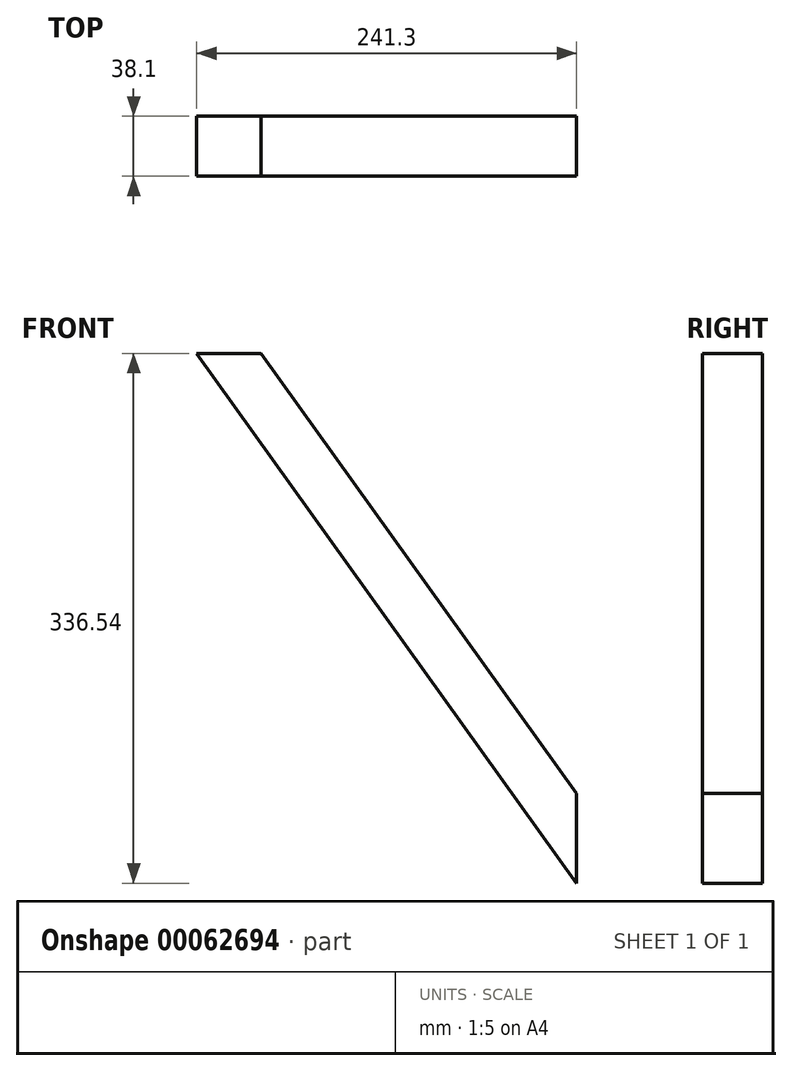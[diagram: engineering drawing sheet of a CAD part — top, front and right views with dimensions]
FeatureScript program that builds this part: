
annotation { "Feature Type Name" : "Feature", "Feature Type Description" : "" }
export const myFeature = defineFeature(function(context is Context, id is Id, definition is map)
    precondition{}
    {
        {
            var Q0;
            Q0=qCreatedBy(makeId("Front.planeOp"),FACE);
            var sketch = newSketch(context, id + "F0", { "sketchPlane" : qUnion([Q0])});
            skLineSegment(sketch, "E0", {"start": v(0, 0) * mm, "end": v(40.83, 0) * mm});
            skLineSegment(sketch, "E1", {"start": v(40.83, 0) * mm, "end": v(241.3, -279.6) * mm});
            skLineSegment(sketch, "E2", {"start": v(241.3, -279.6) * mm, "end": v(241.3, -336.54) * mm});
            skLineSegment(sketch, "E3", {"start": v(241.3, -336.54) * mm, "end": v(0, 0) * mm});
            skLineSegment(sketch, "E4", {"start": v(0, 0) * mm, "end": v(0, -113.1) * mm});
            skSolve(sketch);
        }
        {
            var Q0;
            Q0=makeQuery(id+"F0.imprint","IMPRINT",FACE,{"disambiguationData":[TD([[makeQuery(id+"F0.imprint","IMPRINT",EDGE,{"derivedFrom":sQuery(id+"F0.wireOp",EDGE,"E0")}),-1.0]])]});
            extrude(context, id + "F1", {"entities" : qUnion([Q0]), "depth" : 38.1 * mm});
        }
    });
